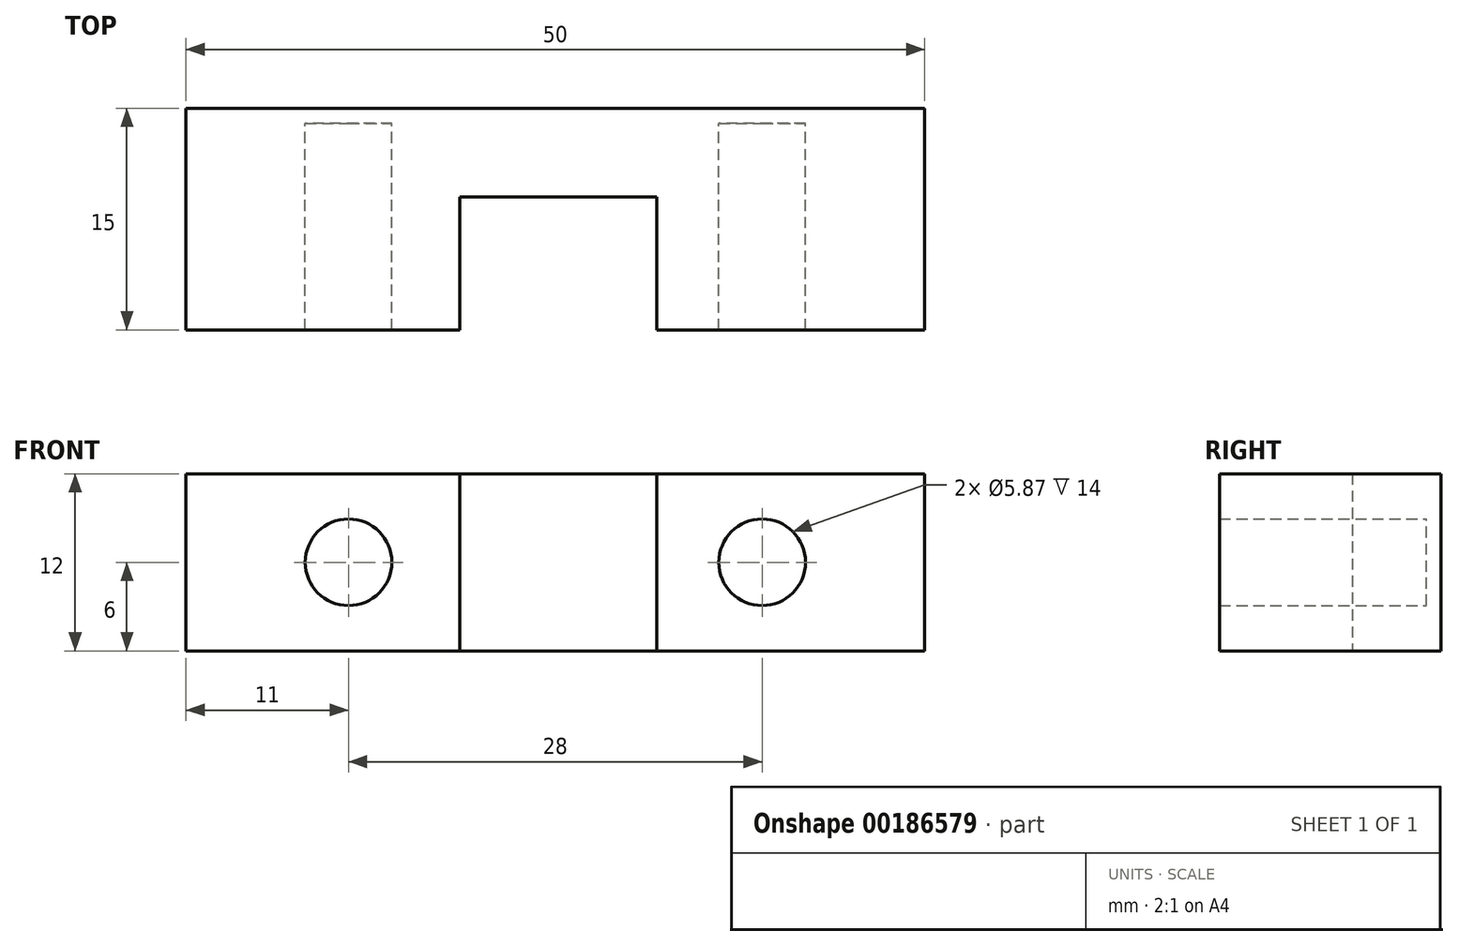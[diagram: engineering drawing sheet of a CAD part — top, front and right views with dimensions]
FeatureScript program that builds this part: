
annotation { "Feature Type Name" : "Feature", "Feature Type Description" : "" }
export const myFeature = defineFeature(function(context is Context, id is Id, definition is map)
    precondition{}
    {
        {
            var Q0;
            Q0=qCreatedBy(makeId("Front.planeOp"),FACE);
            var sketch = newSketch(context, id + "F0", { "sketchPlane" : qUnion([Q0])});
            skLineSegment(sketch, "E0.bottom", {"start": v(25, 6) * mm, "end": v(-25, 6) * mm});
            skLineSegment(sketch, "E0.top", {"start": v(25, -6) * mm, "end": v(-25, -6) * mm});
            skLineSegment(sketch, "E0.left", {"start": v(25, 6) * mm, "end": v(25, -6) * mm});
            skLineSegment(sketch, "E0.right", {"start": v(-25, 6) * mm, "end": v(-25, -6) * mm});
            skPoint(sketch, "E0.middle", {"position": v(0, 0) * mm});
            skCircle(sketch, "E1", {"center": v(-14, 0) * mm, "radius": 2.93 * mm});
            skCircle(sketch, "E2", {"center": v(14, 0) * mm, "radius": 2.93 * mm});
            skPoint(sketch, "E2.centerSnap0", {"position": v(25, 0) * mm});
            skSolve(sketch);
        }
        {
            var Q0;
            Q0 = qSketchRegion(id + "F0", true);
            extrude(context, id + "F1", {"entities" : qUnion([Q0]), "depth" : 5 * mm});
        }
        {
            var Q0;
            Q0=makeQuery(id+"F1.opExtrude","CAP_FACE",FACE,{"disambiguationData":[OSD([sQuery(id+"F0.wireOp",EDGE,"E0.bottom"),sQuery(id+"F0.wireOp",EDGE,"E0.top"),sQuery(id+"F0.wireOp",EDGE,"E0.left"),sQuery(id+"F0.wireOp",EDGE,"E0.right"),sQuery(id+"F0.wireOp",EDGE,"E1"),sQuery(id+"F0.wireOp",EDGE,"E2")])],"isStart":false});
            var sketch = newSketch(context, id + "F2", { "sketchPlane" : qUnion([Q0])});
            skLineSegment(sketch, "E3.bottom", {"start": v(-25, 6) * mm, "end": v(-6.47, 6) * mm});
            skLineSegment(sketch, "E3.top", {"start": v(-25, -6) * mm, "end": v(-6.47, -6) * mm});
            skLineSegment(sketch, "E3.left", {"start": v(-25, 6) * mm, "end": v(-25, -6) * mm});
            skLineSegment(sketch, "E3.right", {"start": v(-6.47, 6) * mm, "end": v(-6.47, -6) * mm});
            skLineSegment(sketch, "E4.bottom", {"start": v(25, 6) * mm, "end": v(6.88, 6) * mm});
            skLineSegment(sketch, "E4.top", {"start": v(25, -6) * mm, "end": v(6.88, -6) * mm});
            skLineSegment(sketch, "E4.left", {"start": v(25, 6) * mm, "end": v(25, -6) * mm});
            skLineSegment(sketch, "E4.right", {"start": v(6.88, 6) * mm, "end": v(6.88, -6) * mm});
            skSolve(sketch);
        }
        {
            var Q0;
            Q0 = qSketchRegion(id + "F2", true);
            extrude(context, id + "F3", {"entities" : qUnion([Q0]), "operationType" : NewBodyOperationType.ADD, "depth" : 9 * mm});
        }
        {
            var Q0;
            Q0=makeQuery(id+"F1.opExtrude","CAP_FACE",FACE,{"disambiguationData":[OSD([sQuery(id+"F0.wireOp",EDGE,"E0.bottom"),sQuery(id+"F0.wireOp",EDGE,"E0.top"),sQuery(id+"F0.wireOp",EDGE,"E0.left"),sQuery(id+"F0.wireOp",EDGE,"E0.right"),sQuery(id+"F0.wireOp",EDGE,"E1"),sQuery(id+"F0.wireOp",EDGE,"E2")])],"isStart":true});
            var sketch = newSketch(context, id + "F4", { "sketchPlane" : qUnion([Q0])});
            skCircle(sketch, "E5", {"center": v(-14, 0) * mm, "radius": 2.93 * mm});
            skCircle(sketch, "E6", {"center": v(14, 0) * mm, "radius": 2.93 * mm});
            skSolve(sketch);
        }
        {
            var Q0;
            Q0 = qSketchRegion(id + "F4", true);
            extrude(context, id + "F5", {"entities" : qUnion([Q0]), "operationType" : NewBodyOperationType.REMOVE, "oppositeDirection" : true, "depth" : 25 * mm});
        }
        {
            var Q0;
            Q0=makeQuery(id+"F1.opExtrude","CAP_FACE",FACE,{"disambiguationData":[OSD([sQuery(id+"F0.wireOp",EDGE,"E0.bottom"),sQuery(id+"F0.wireOp",EDGE,"E0.top"),sQuery(id+"F0.wireOp",EDGE,"E0.left"),sQuery(id+"F0.wireOp",EDGE,"E0.right"),sQuery(id+"F0.wireOp",EDGE,"E1"),sQuery(id+"F0.wireOp",EDGE,"E2")])],"isStart":true});
            var sketch = newSketch(context, id + "F6", { "sketchPlane" : qUnion([Q0])});
            skLineSegment(sketch, "E7.bottom", {"start": v(-25, 6) * mm, "end": v(25, 6) * mm});
            skLineSegment(sketch, "E7.top", {"start": v(-25, -6) * mm, "end": v(25, -6) * mm});
            skLineSegment(sketch, "E7.left", {"start": v(-25, 6) * mm, "end": v(-25, -6) * mm});
            skLineSegment(sketch, "E7.right", {"start": v(25, 6) * mm, "end": v(25, -6) * mm});
            skSolve(sketch);
        }
        {
            var Q0;
            Q0 = qSketchRegion(id + "F6", true);
            extrude(context, id + "F7", {"entities" : qUnion([Q0]), "operationType" : NewBodyOperationType.ADD, "depth" : 1 * mm});
        }
    });
